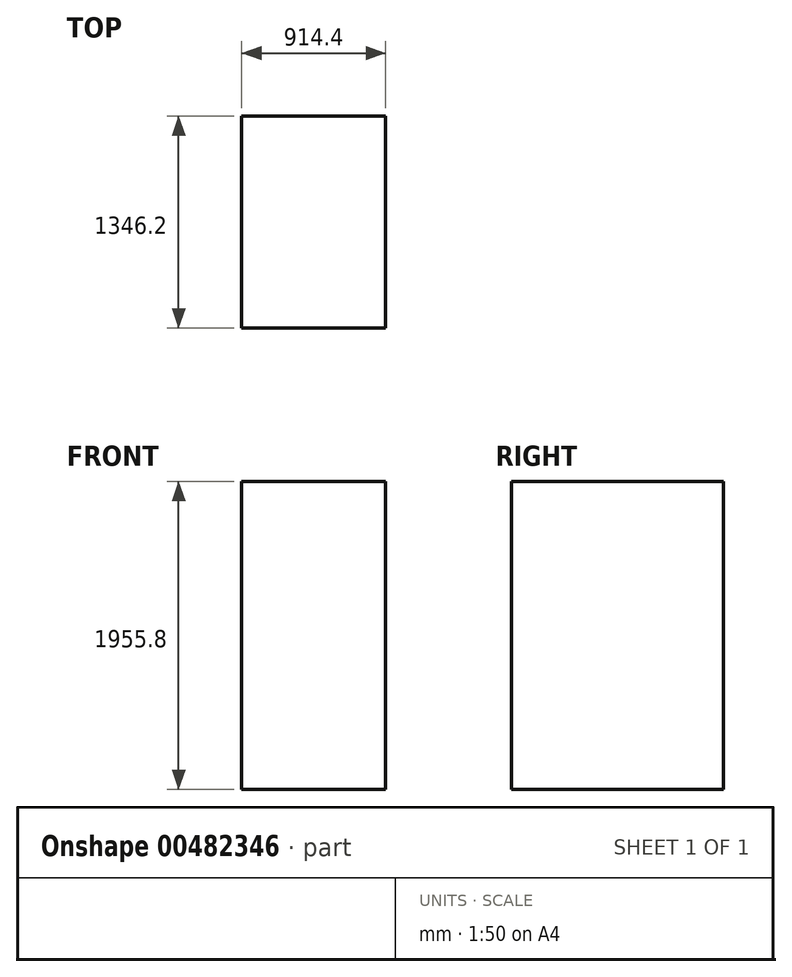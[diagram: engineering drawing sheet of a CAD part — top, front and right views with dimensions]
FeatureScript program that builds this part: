
annotation { "Feature Type Name" : "Feature", "Feature Type Description" : "" }
export const myFeature = defineFeature(function(context is Context, id is Id, definition is map)
    precondition{}
    {
        {
            var Q0;
            Q0=qCreatedBy(makeId("Top.planeOp"),FACE);
            var sketch = newSketch(context, id + "F0", { "sketchPlane" : qUnion([Q0])});
            skLineSegment(sketch, "E0.bottom", {"start": v(0, 0) * mm, "end": v(914.4, 0) * mm});
            skLineSegment(sketch, "E0.top", {"start": v(0, 1346.2) * mm, "end": v(914.4, 1346.2) * mm});
            skLineSegment(sketch, "E0.left", {"start": v(0, 0) * mm, "end": v(0, 1346.2) * mm});
            skLineSegment(sketch, "E0.right", {"start": v(914.4, 0) * mm, "end": v(914.4, 1346.2) * mm});
            skSolve(sketch);
        }
        {
            var Q0;
            Q0 = qSketchRegion(id + "F0", true);
            extrude(context, id + "F1", {"entities" : qUnion([Q0]), "depth" : 1955.8 * mm, "offsetDistance" : 25.4 * mm});
        }
    });
